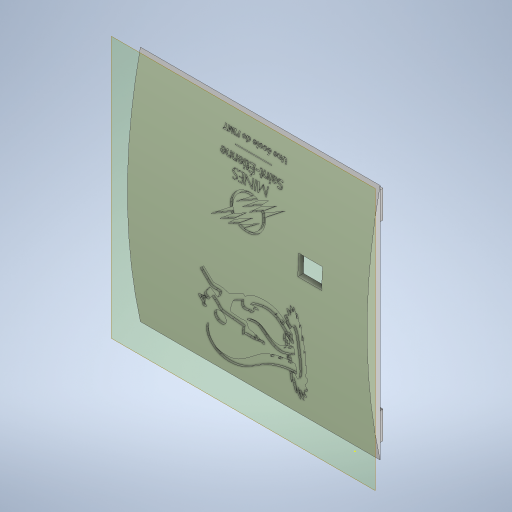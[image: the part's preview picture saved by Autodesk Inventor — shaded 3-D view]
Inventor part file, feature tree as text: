
AUTODESK INVENTOR PART (.ipt)
format: ipt  version: 2023 (Build 270158000, 158)  size: 7,538,176 bytes
history: native  units: mm
features: sketch x10, extrude x7, other x3
ambient origin geometry x8: Origin, YZ Plane, XZ Plane, XY Plane, X Axis, Y Axis, Z Axis, Center Point
bodies: Solide1 (feature_tree)
feature tree (20):
  extrude  "Extrusion1"  Depth=118.0mm
  extrude  "Extrusion2"  Depth=113.0mm
  extrude  "Extrusion3"  Depth=3.0mm
  extrude  "Extrusion4"  Depth=3.0mm
  extrude  "Extrusion5"  Depth=3.0mm
  extrude  "Extrusion6"  Depth=3.0mm
  other  "Plan de construction1"
  sketch  "Esquisse7"
  extrude  "Extrusion7"  Depth=1.3mm
  other  "Gravure1"
  other  "Gravure2"
  sketch  "Esquisse1"
  sketch  "Esquisse2"
  sketch  "Esquisse3"
  sketch  "Esquisse4"
  sketch  "Esquisse5"
  sketch  "Esquisse6"
  sketch  "Esquisse8"
  sketch  "Esquisse9"
  sketch  "Esquisse10"
